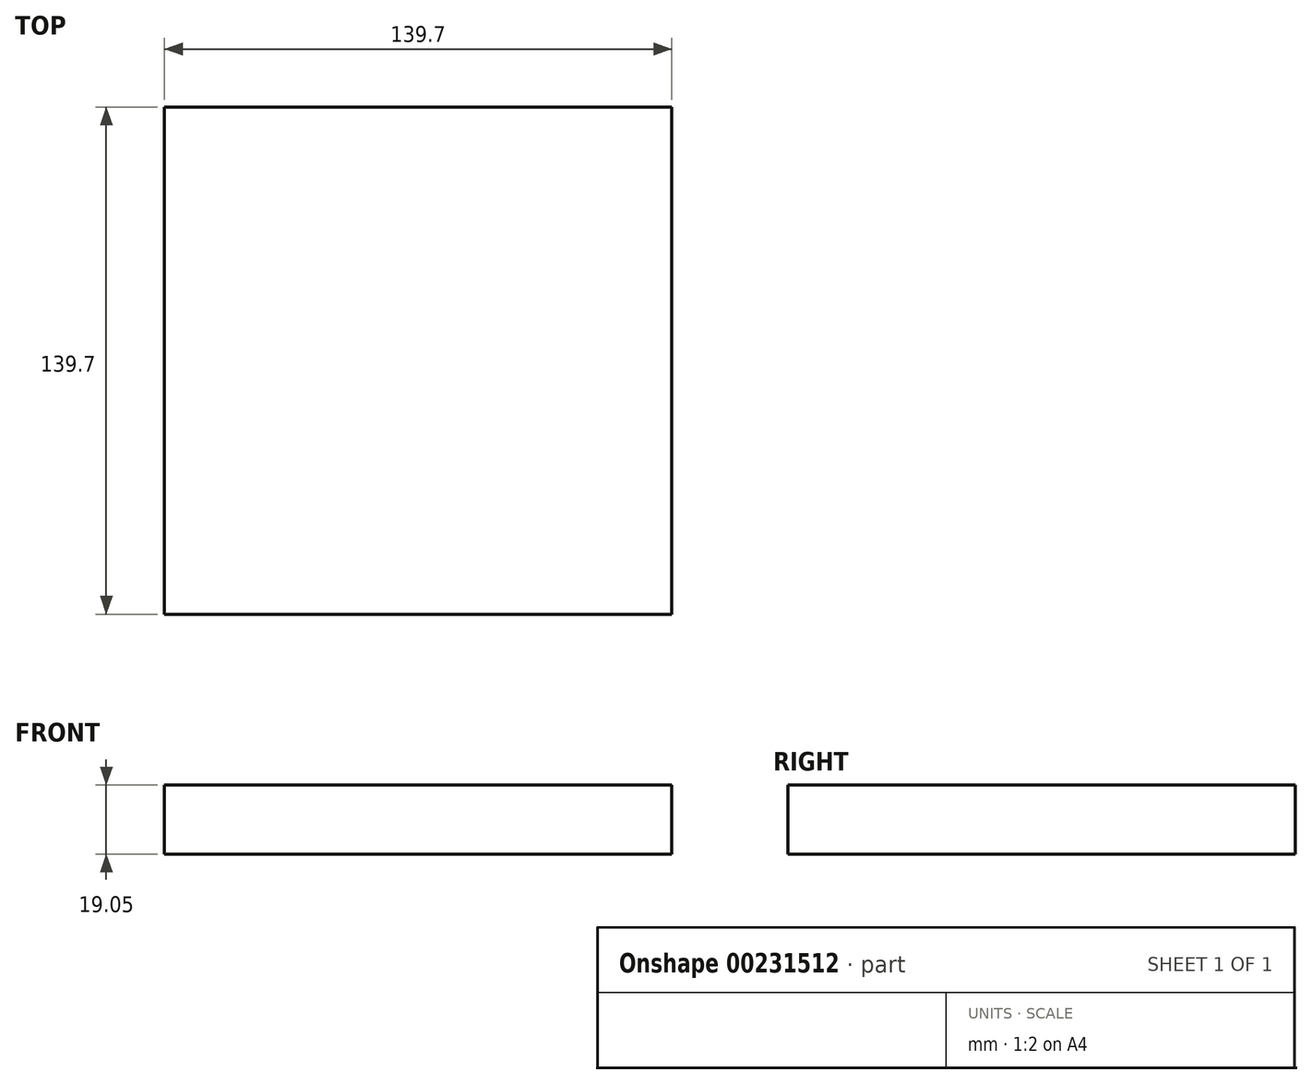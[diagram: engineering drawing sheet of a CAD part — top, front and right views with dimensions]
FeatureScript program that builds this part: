
annotation { "Feature Type Name" : "Feature", "Feature Type Description" : "" }
export const myFeature = defineFeature(function(context is Context, id is Id, definition is map)
    precondition{}
    {
        {
            var Q0;
            Q0=qCreatedBy(makeId("Top.planeOp"),FACE);
            var sketch = newSketch(context, id + "F0", { "sketchPlane" : qUnion([Q0])});
            skLineSegment(sketch, "E0.bottom", {"start": v(-69.85, -69.85) * mm, "end": v(69.85, -69.85) * mm});
            skLineSegment(sketch, "E0.top", {"start": v(-69.85, 69.85) * mm, "end": v(69.85, 69.85) * mm});
            skLineSegment(sketch, "E0.left", {"start": v(-69.85, -69.85) * mm, "end": v(-69.85, 69.85) * mm});
            skLineSegment(sketch, "E0.right", {"start": v(69.85, -69.85) * mm, "end": v(69.85, 69.85) * mm});
            skPoint(sketch, "E0.middle", {"position": v(0, 0) * mm});
            skLineSegment(sketch, "E1", {"start": v(0, -69.85) * mm, "end": v(0, -63.5) * mm});
            skPoint(sketch, "E1.endSnap0", {"position": v(0, -69.85) * mm});
            skCircle(sketch, "E2", {"center": v(0, -63.5) * mm, "radius": 6.35 * mm});
            skSolve(sketch);
        }
        {
            var Q0;
            Q0 = qSketchRegion(id + "F0", true);
            extrude(context, id + "F1", {"entities" : qUnion([Q0]), "depth" : 19.05 * mm});
        }
    });
